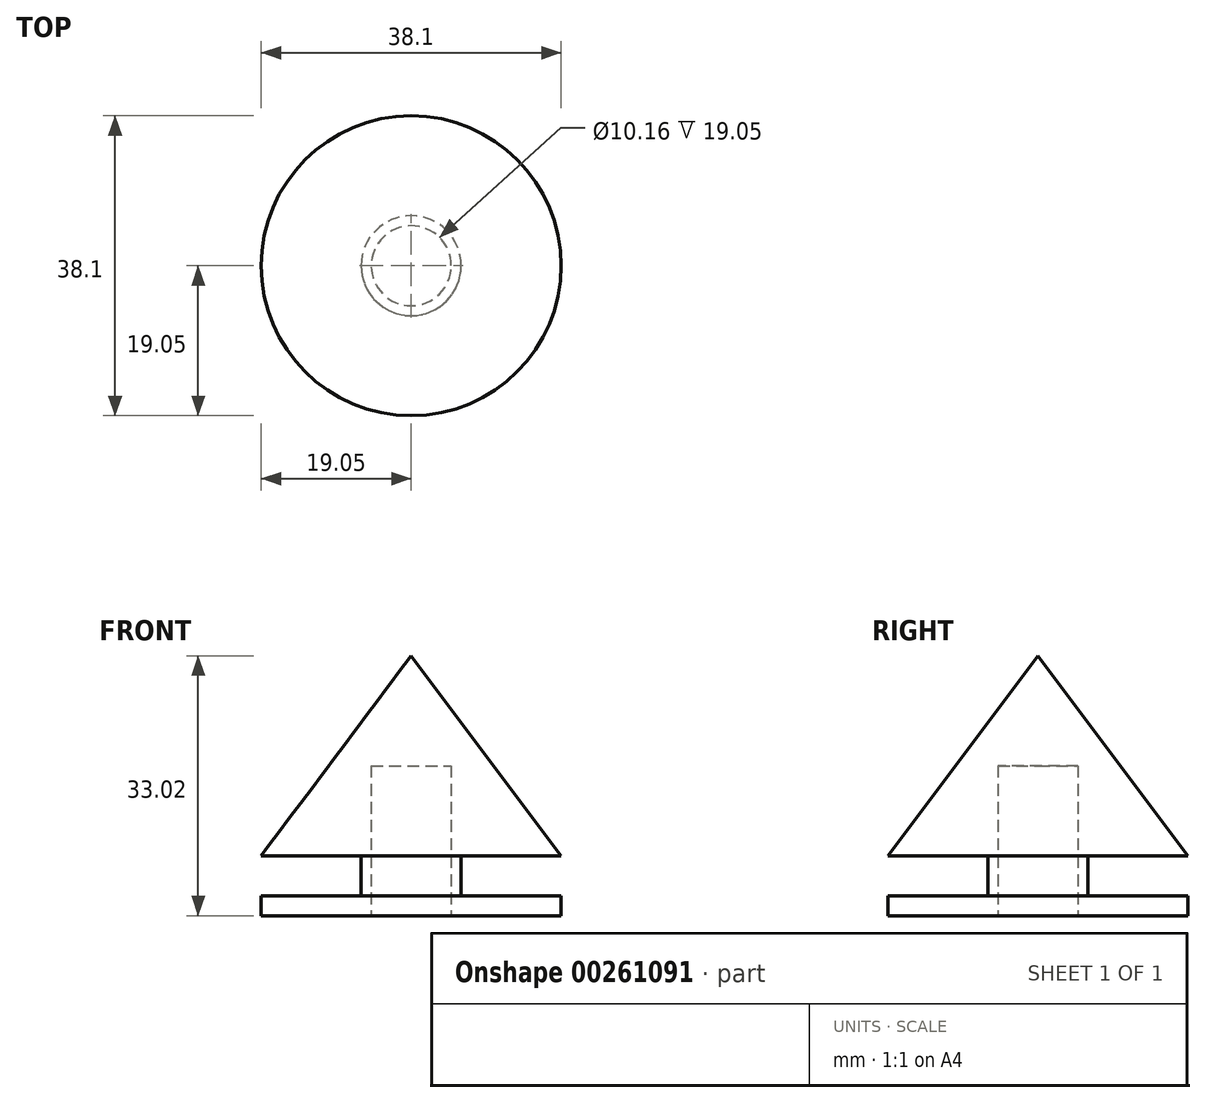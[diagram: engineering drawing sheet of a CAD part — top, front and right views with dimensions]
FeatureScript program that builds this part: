
annotation { "Feature Type Name" : "Feature", "Feature Type Description" : "" }
export const myFeature = defineFeature(function(context is Context, id is Id, definition is map)
    precondition{}
    {
        {
            var Q0;
            Q0=qCreatedBy(makeId("Top.planeOp"),FACE);
            var sketch = newSketch(context, id + "F0", { "sketchPlane" : qUnion([Q0])});
            skCircle(sketch, "E0", {"center": v(0, 0) * mm, "radius": 19.05 * mm});
            skSolve(sketch);
        }
        {
            var Q0;
            Q0=qCreatedBy(makeId("Front.planeOp"),FACE);
            var sketch = newSketch(context, id + "F1", { "sketchPlane" : qUnion([Q0])});
            skLineSegment(sketch, "E1", {"start": v(0, 0) * mm, "end": v(0, 25.4) * mm});
            skLineSegment(sketch, "E2", {"start": v(0, 0) * mm, "end": v(-19.05, 0) * mm});
            skLineSegment(sketch, "E3", {"start": v(-19.05, 0) * mm, "end": v(0, 25.4) * mm});
            skLineSegment(sketch, "E4.MirrorCS", {"start": v(19.05, 0) * mm, "end": v(0, 25.4) * mm});
            skLineSegment(sketch, "E5.MirrorCS", {"start": v(0, 0) * mm, "end": v(19.05, 0) * mm});
            skSolve(sketch);
        }
        {
            var Q0;
            Q0=makeQuery(id+"F1.imprint","IMPRINT",FACE,{"disambiguationData":[TD([[makeQuery(id+"F1.imprint","IMPRINT",EDGE,{"derivedFrom":sQuery(id+"F1.wireOp",EDGE,"E1")}),-1.0]])]});
            var Q1;
            Q1=sQuery(id+"F1.wireOp",EDGE,"E1");
            revolve(context, id + "F2", {"entities" : qUnion([Q0]), "axis" : qUnion([Q1]), "revolveType" : RevolveType.FULL});
        }
        {
            var Q0;
            Q0=makeQuery(id+"F0.imprint","IMPRINT",FACE,{"disambiguationData":[TD([[makeQuery(id+"F0.imprint","IMPRINT",EDGE,{"derivedFrom":sQuery(id+"F0.wireOp",EDGE,"E0")}),1.0]])]});
            var sketch = newSketch(context, id + "F3", { "sketchPlane" : qUnion([Q0])});
            skCircle(sketch, "E6", {"center": v(0, 0) * mm, "radius": 6.35 * mm});
            skSolve(sketch);
        }
        {
            var Q0;
            Q0 = qSketchRegion(id + "F3", true);
            extrude(context, id + "F4", {"entities" : qUnion([Q0]), "operationType" : NewBodyOperationType.ADD, "oppositeDirection" : true, "depth" : 5.08 * mm});
        }
        {
            var Q0;
            Q0=makeQuery(id+"F4.opExtrude","CAP_FACE",FACE,{"disambiguationData":[OSD([sQuery(id+"F3.wireOp",EDGE,"E6")])],"isStart":false});
            var sketch = newSketch(context, id + "F5", { "sketchPlane" : qUnion([Q0])});
            skCircle(sketch, "E7", {"center": v(0, 0) * mm, "radius": 19.05 * mm});
            skSolve(sketch);
        }
        {
            var Q0;
            Q0=makeQuery(id+"F5.imprint","IMPRINT",FACE,{"disambiguationData":[TD([[makeQuery(id+"F5.imprint","IMPRINT",EDGE,{"derivedFrom":sQuery(id+"F5.wireOp",EDGE,"E7")}),1.0]])]});
            var Q1;
            Q1=makeQuery(id+"F5.imprint","IMPRINT",FACE,{"disambiguationData":[TD([[makeQuery(id+"F5.imprint","IMPRINT",EDGE,{"derivedFrom":makeQuery(id+"F4.opExtrude","CAP_EDGE",EDGE,{"disambiguationData":[OSD([sQuery(id+"F3.wireOp",EDGE,"E6")])],"isStart":false})}),-1.0]])]});
            extrude(context, id + "F6", {"entities" : qUnion([Q0, Q1]), "operationType" : NewBodyOperationType.ADD, "depth" : 2.54 * mm});
        }
        {
            var Q0;
            Q0=makeQuery(id+"F6.opExtrude","CAP_FACE",FACE,{"disambiguationData":[OSD([sQuery(id+"F5.wireOp",EDGE,"E7")])],"isStart":false});
            var sketch = newSketch(context, id + "F7", { "sketchPlane" : qUnion([Q0])});
            skCircle(sketch, "E8", {"center": v(0, 0) * mm, "radius": 5.08 * mm});
            skSolve(sketch);
        }
        {
            var Q0;
            Q0=makeQuery(id+"F7.imprint","IMPRINT",FACE,{"disambiguationData":[TD([[makeQuery(id+"F7.imprint","IMPRINT",EDGE,{"derivedFrom":sQuery(id+"F7.wireOp",EDGE,"E8")}),1.0]])]});
            extrude(context, id + "F8", {"entities" : qUnion([Q0]), "operationType" : NewBodyOperationType.REMOVE, "oppositeDirection" : true, "depth" : 19.05 * mm});
        }
    });
